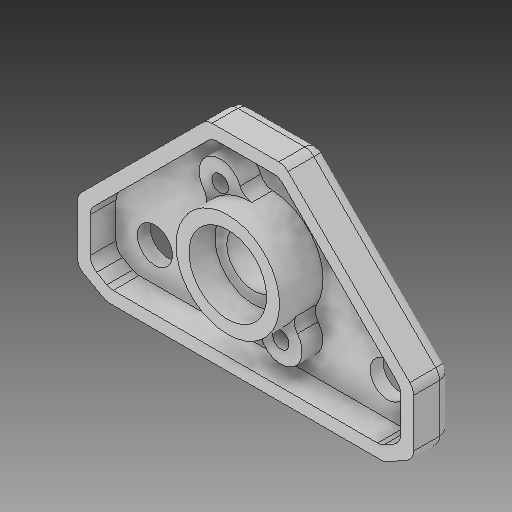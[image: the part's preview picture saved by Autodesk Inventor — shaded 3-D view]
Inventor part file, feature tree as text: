
AUTODESK INVENTOR PART (.ipt)
format: ipt  version: 2017 (Build 210142000, 142)  size: 202,752 bytes
history: native  units: in
note: dims shown in document units (in); Inventor stores cm internally (conversion verified against a paired STEP export)
features: fillet x1
ambient origin geometry x8: Origin, YZ Plane, XZ Plane, XY Plane, X Axis, Y Axis, Z Axis, Center Point
bodies: Solid1 (feature_tree)
feature tree (1):
  fillet  "Fillet2"  [1 undecoded]
note: 1 required parameter value undecoded (feature->parameter linkage not recoverable at this tier; creation-order binding heuristic only, values carry confidence <= 0.55)
